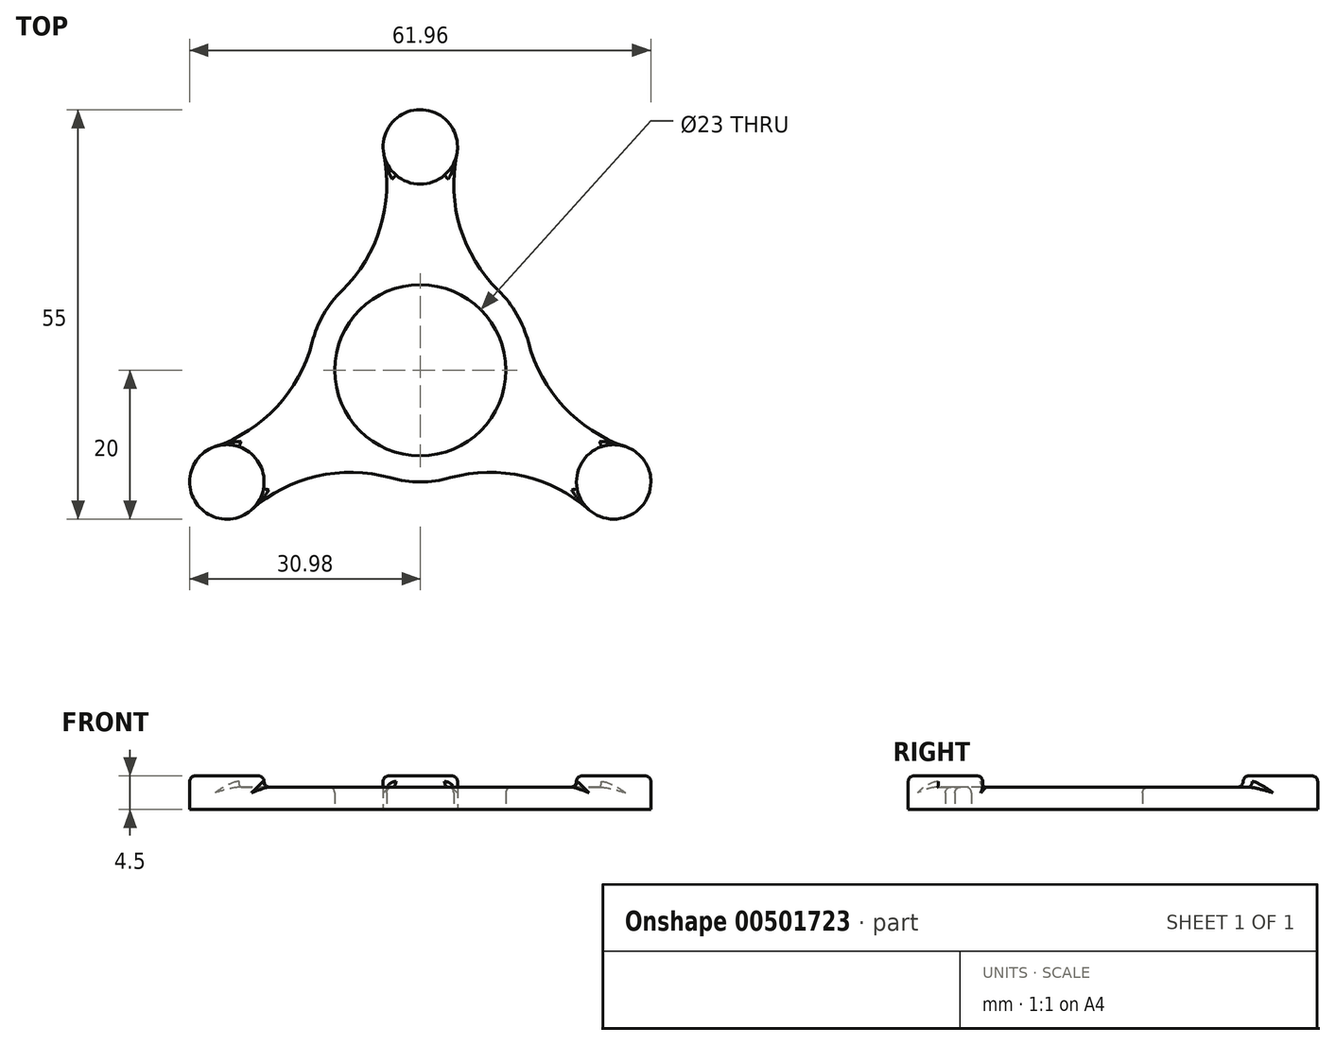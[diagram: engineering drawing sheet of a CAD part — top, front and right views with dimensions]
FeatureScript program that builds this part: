
annotation { "Feature Type Name" : "Feature", "Feature Type Description" : "" }
export const myFeature = defineFeature(function(context is Context, id is Id, definition is map)
    precondition{}
    {
        {
            var Q0;
            Q0=qCreatedBy(makeId("Top.planeOp"),FACE);
            var sketch = newSketch(context, id + "F0", { "sketchPlane" : qUnion([Q0])});
            skCircle(sketch, "E0", {"center": v(0, 0) * mm, "radius": 11.5 * mm});
            skArc(sketch, "E1", {"start": v(-10.5, 10.71) * mm, "mid": v(-13, 7.5) * mm, "end": v(-14.53, 3.73) * mm});
            skCircle(sketch, "E2", {"center": v(0, 30) * mm, "radius": 5 * mm});
            skArc(sketch, "E3", {"start": v(-10.5, 10.71) * mm, "mid": v(-5.37, 19.14) * mm, "end": v(-4.9, 29) * mm});
            skArc(sketch, "E4", {"start": v(4.9, 29) * mm, "mid": v(5.37, 19.14) * mm, "end": v(10.5, 10.71) * mm});
            skArc(sketch, "E5.1.0", {"start": v(-4.03, -14.45) * mm, "mid": v(-13.9, -14.22) * mm, "end": v(-22.67, -18.74) * mm});
            skCircle(sketch, "E5.1.1", {"center": v(-25.98, -15) * mm, "radius": 5 * mm});
            skArc(sketch, "E5.1.2", {"start": v(-27.56, -10.26) * mm, "mid": v(-19.27, -4.92) * mm, "end": v(-14.53, 3.73) * mm});
            skArc(sketch, "E5.2.0", {"start": v(14.53, 3.73) * mm, "mid": v(19.27, -4.92) * mm, "end": v(27.56, -10.26) * mm});
            skCircle(sketch, "E5.2.1", {"center": v(25.98, -15) * mm, "radius": 5 * mm});
            skArc(sketch, "E5.2.2", {"start": v(22.67, -18.74) * mm, "mid": v(13.9, -14.22) * mm, "end": v(4.03, -14.45) * mm});
            skArc(sketch, "E6.trimOffspring", {"start": v(-4.03, -14.45) * mm, "mid": v(0, -15) * mm, "end": v(4.03, -14.45) * mm});
            skArc(sketch, "E7.trimOffspring", {"start": v(14.53, 3.73) * mm, "mid": v(13, 7.5) * mm, "end": v(10.5, 10.71) * mm});
            skSolve(sketch);
        }
        {
            var Q0;
            Q0=makeQuery(id+"F0.imprint","IMPRINT",FACE,{"disambiguationData":[TD([[makeQuery(id+"F0.imprint","IMPRINT",EDGE,{"derivedFrom":sQuery(id+"F0.wireOp",EDGE,"E0")}),-1.0]])]});
            extrude(context, id + "F1", {"entities" : qUnion([Q0]), "depth" : 3 * mm});
        }
        {
            var Q0;
            {var subQ0=sQuery(id+"F0.wireOp",EDGE,"E5.2.1");var subQ1=makeQuery(id+"F0.imprint","INTERSECT",VERTEX,{"derivedFrom":[sQuery(id+"F0.wireOp",EDGE,"E5.2.0"),subQ0]});Q0=makeQuery(id+"F0.imprint","IMPRINT",FACE,{"disambiguationData":[TD([[makeQuery(id+"F0.imprint","IMPRINT",EDGE,{"disambiguationData":[TD([[subQ1,-1.0]])],"derivedFrom":subQ0}),1.0]])]});}
            var Q1;
            {var subQ0=sQuery(id+"F0.wireOp",EDGE,"E5.1.1");var subQ1=makeQuery(id+"F0.imprint","INTERSECT",VERTEX,{"derivedFrom":[sQuery(id+"F0.wireOp",EDGE,"E5.1.0"),subQ0]});Q1=makeQuery(id+"F0.imprint","IMPRINT",FACE,{"disambiguationData":[TD([[makeQuery(id+"F0.imprint","IMPRINT",EDGE,{"disambiguationData":[TD([[subQ1,-1.0]])],"derivedFrom":subQ0}),1.0]])]});}
            var Q2;
            {var subQ0=sQuery(id+"F0.wireOp",EDGE,"E2");var subQ1=makeQuery(id+"F0.imprint","INTERSECT",VERTEX,{"derivedFrom":[subQ0,sQuery(id+"F0.wireOp",EDGE,"E3")]});Q2=makeQuery(id+"F0.imprint","IMPRINT",FACE,{"disambiguationData":[TD([[makeQuery(id+"F0.imprint","IMPRINT",EDGE,{"disambiguationData":[TD([[subQ1,-1.0]])],"derivedFrom":subQ0}),1.0]])]});}
            extrude(context, id + "F2", {"entities" : qUnion([Q0, Q1, Q2]), "operationType" : NewBodyOperationType.ADD, "depth" : 4.5 * mm});
        }
        {
            var Q0;
            Q0=makeQuery(id+"F1.opExtrude","CAP_EDGE",EDGE,{"disambiguationData":[OSD([sQuery(id+"F0.wireOp",EDGE,"E2")])],"isStart":false});
            var Q1;
            Q1=makeQuery(id+"F2.opExtrude","CAP_FACE",FACE,{"disambiguationData":[OSD([sQuery(id+"F0.wireOp",EDGE,"E2")])],"isStart":false});
            var Q2;
            Q2=makeQuery(id+"F1.opExtrude","CAP_EDGE",EDGE,{"disambiguationData":[OSD([sQuery(id+"F0.wireOp",EDGE,"E5.1.1")])],"isStart":false});
            var Q3;
            Q3=makeQuery(id+"F2.opExtrude","CAP_EDGE",EDGE,{"disambiguationData":[OSD([sQuery(id+"F0.wireOp",EDGE,"E5.1.1")])],"isStart":false});
            var Q4;
            Q4=makeQuery(id+"F1.opExtrude","CAP_EDGE",EDGE,{"disambiguationData":[OSD([sQuery(id+"F0.wireOp",EDGE,"E5.2.1")])],"isStart":false});
            var Q5;
            Q5=makeQuery(id+"F2.opExtrude","CAP_EDGE",EDGE,{"disambiguationData":[OSD([sQuery(id+"F0.wireOp",EDGE,"E5.2.1")])],"isStart":false});
            fillet(context, id + "F3", {"entities" : qUnion([Q0, Q1, Q2, Q3, Q4, Q5]), "radius" : 0.75 * mm, "tangentPropagation" : true, "allowEdgeOverflow" : false});
        }
        {
            var Q0;
            Q0=makeQuery(id+"F1.opExtrude","CAP_FACE",FACE,{"disambiguationData":[OSD([sQuery(id+"F0.wireOp",EDGE,"E0"),sQuery(id+"F0.wireOp",EDGE,"E1"),sQuery(id+"F0.wireOp",EDGE,"E2"),sQuery(id+"F0.wireOp",EDGE,"E3"),sQuery(id+"F0.wireOp",EDGE,"E4"),sQuery(id+"F0.wireOp",EDGE,"E5.1.0"),sQuery(id+"F0.wireOp",EDGE,"E5.1.1"),sQuery(id+"F0.wireOp",EDGE,"E5.1.2"),sQuery(id+"F0.wireOp",EDGE,"E5.2.0"),sQuery(id+"F0.wireOp",EDGE,"E5.2.1"),sQuery(id+"F0.wireOp",EDGE,"E5.2.2"),sQuery(id+"F0.wireOp",EDGE,"E6.trimOffspring"),sQuery(id+"F0.wireOp",EDGE,"E7.trimOffspring")])],"isStart":false});
            fillet(context, id + "F4", {"entities" : qUnion([Q0]), "radius" : 0.75 * mm, "tangentPropagation" : true, "allowEdgeOverflow" : false});
        }
    });
